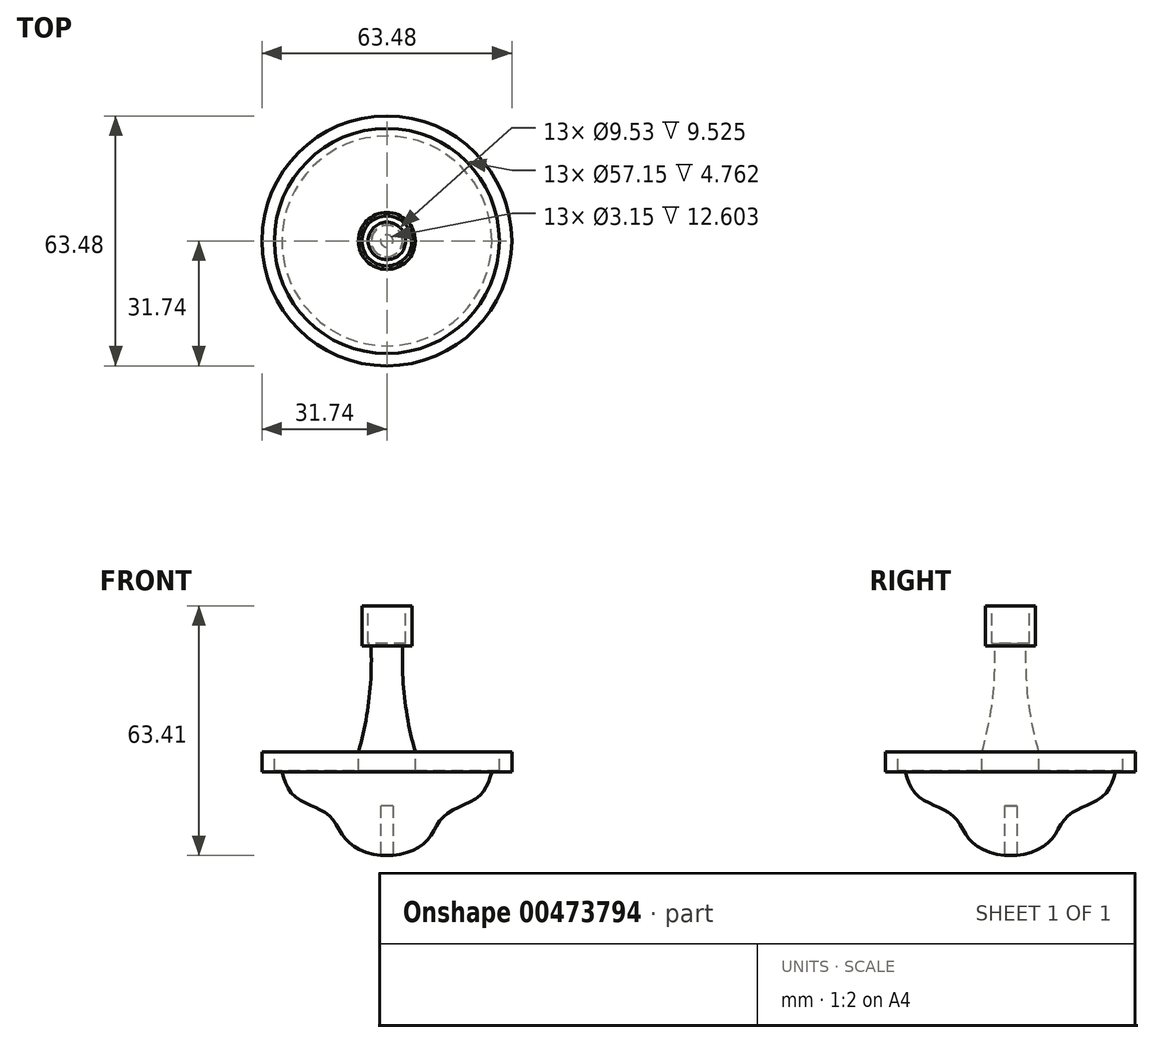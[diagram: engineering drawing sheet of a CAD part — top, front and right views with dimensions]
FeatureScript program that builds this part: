
annotation { "Feature Type Name" : "Feature", "Feature Type Description" : "" }
export const myFeature = defineFeature(function(context is Context, id is Id, definition is map)
    precondition{}
    {
        {
            var Q0;
            Q0=qCreatedBy(makeId("Front.planeOp"),FACE);
            var sketch = newSketch(context, id + "F0", { "sketchPlane" : qUnion([Q0])});
            skLineSegment(sketch, "E0", {"start": v(0, 30.66) * mm, "end": v(0, -32.84) * mm});
            skLineSegment(sketch, "E1", {"start": v(0, 30.66) * mm, "end": v(6.35, 30.66) * mm});
            skLineSegment(sketch, "E2", {"start": v(6.35, 30.66) * mm, "end": v(6.35, 20.5) * mm});
            skLineSegment(sketch, "E3", {"start": v(6.35, 20.5) * mm, "end": v(4.02, 20.5) * mm});
            skArc(sketch, "E4", {"start": v(4.02, 20.5) * mm, "mid": v(4.54, 6.89) * mm, "end": v(7.23, -6.46) * mm});
            skLineSegment(sketch, "E5", {"start": v(7.23, -6.46) * mm, "end": v(31.74, -6.46) * mm});
            skLineSegment(sketch, "E6", {"start": v(31.74, -6.46) * mm, "end": v(31.74, -11.54) * mm});
            skLineSegment(sketch, "E7", {"start": v(31.74, -11.54) * mm, "end": v(26.66, -11.54) * mm});
            skFitSpline(sketch, "E8", {"points": [v(26.66, -11.54) * mm, v(23.27, -17.82) * mm, v(14.8, -22.5) * mm, v(10.12, -28.97) * mm, v(0, -32.84) * mm], "startDerivative": vector(-9.24, -31.9) * mm, "endDerivative": vector(-46.88, -1.05) * mm});
            skSolve(sketch);
        }
        {
            var Q0;
            Q0=makeQuery(id+"F0.imprint","IMPRINT",FACE,{"disambiguationData":[TD([[makeQuery(id+"F0.imprint","IMPRINT",EDGE,{"derivedFrom":sQuery(id+"F0.wireOp",EDGE,"E0")}),1.0]])]});
            var Q1;
            Q1=sQuery(id+"F0.wireOp",EDGE,"E0");
            revolve(context, id + "F1", {"entities" : qUnion([Q0]), "axis" : qUnion([Q1]), "revolveType" : RevolveType.FULL});
        }
        {
            var Q0;
            Q0=makeQuery(id+"F1.opRevolve","SWEPT_FACE",FACE,{"disambiguationData":[OSD([sQuery(id+"F0.wireOp",EDGE,"E1")])]});
            var sketch = newSketch(context, id + "F2", { "sketchPlane" : qUnion([Q0])});
            skCircle(sketch, "E9", {"center": v(0, 0) * mm, "radius": 4.76 * mm});
            skSolve(sketch);
        }
        {
            var Q0;
            Q0=makeQuery(id+"F2.imprint","IMPRINT",FACE,{"disambiguationData":[TD([[makeQuery(id+"F2.imprint","IMPRINT",EDGE,{"derivedFrom":sQuery(id+"F2.wireOp",EDGE,"E9")}),1.0]])]});
            var Q1;
            Q1=sQuery(id+"F2.wireOp",EDGE,"E9");
            extrude(context, id + "F3", {"entities" : qUnion([Q0]), "operationType" : NewBodyOperationType.REMOVE, "surfaceEntities" : qUnion([Q1]), "oppositeDirection" : true, "depth" : 9.52 * mm});
        }
        {
            var Q0;
            Q0=makeQuery(id+"F1.opRevolve","SWEPT_FACE",FACE,{"disambiguationData":[OSD([sQuery(id+"F0.wireOp",EDGE,"E5")])]});
            var sketch = newSketch(context, id + "F4", { "sketchPlane" : qUnion([Q0])});
            skCircle(sketch, "E10", {"center": v(0, 0) * mm, "radius": 28.58 * mm});
            skSolve(sketch);
        }
        {
            var Q0;
            Q0=makeQuery(id+"F4.imprint","IMPRINT",FACE,{"disambiguationData":[TD([[makeQuery(id+"F4.imprint","IMPRINT",EDGE,{"derivedFrom":sQuery(id+"F4.wireOp",EDGE,"E10")}),1.0]])]});
            var Q1;
            Q1=sQuery(id+"F4.wireOp",EDGE,"E10");
            extrude(context, id + "F5", {"entities" : qUnion([Q0]), "operationType" : NewBodyOperationType.REMOVE, "surfaceEntities" : qUnion([Q1]), "oppositeDirection" : true, "depth" : 4.76 * mm});
        }
        {
            var Q0;
            Q0=qCreatedBy(makeId("Top.planeOp"),FACE);
            cPlane(context, id + "F6", {"entities" : qUnion([Q0]), "cplaneType" : CPlaneType.OFFSET, "offset" : 32.84 * mm, "oppositeDirection" : true, "width" : 152.4 * mm, "height" : 152.4 * mm});
        }
        {
            var Q0;
            Q0=qCreatedBy(id+"F6.planeOp",FACE);
            var sketch = newSketch(context, id + "F7", { "sketchPlane" : qUnion([Q0])});
            skCircle(sketch, "E11", {"center": v(0, 0) * mm, "radius": 1.57 * mm});
            skSolve(sketch);
        }
        {
            var Q0;
            Q0=makeQuery(id+"F7.imprint","IMPRINT",FACE,{"disambiguationData":[TD([[makeQuery(id+"F7.imprint","IMPRINT",EDGE,{"derivedFrom":sQuery(id+"F7.wireOp",EDGE,"E11")}),1.0]])]});
            var Q1;
            Q1=sQuery(id+"F7.wireOp",EDGE,"E11");
            extrude(context, id + "F8", {"entities" : qUnion([Q0]), "operationType" : NewBodyOperationType.REMOVE, "surfaceEntities" : qUnion([Q1]), "depth" : 12.7 * mm});
        }
    });
